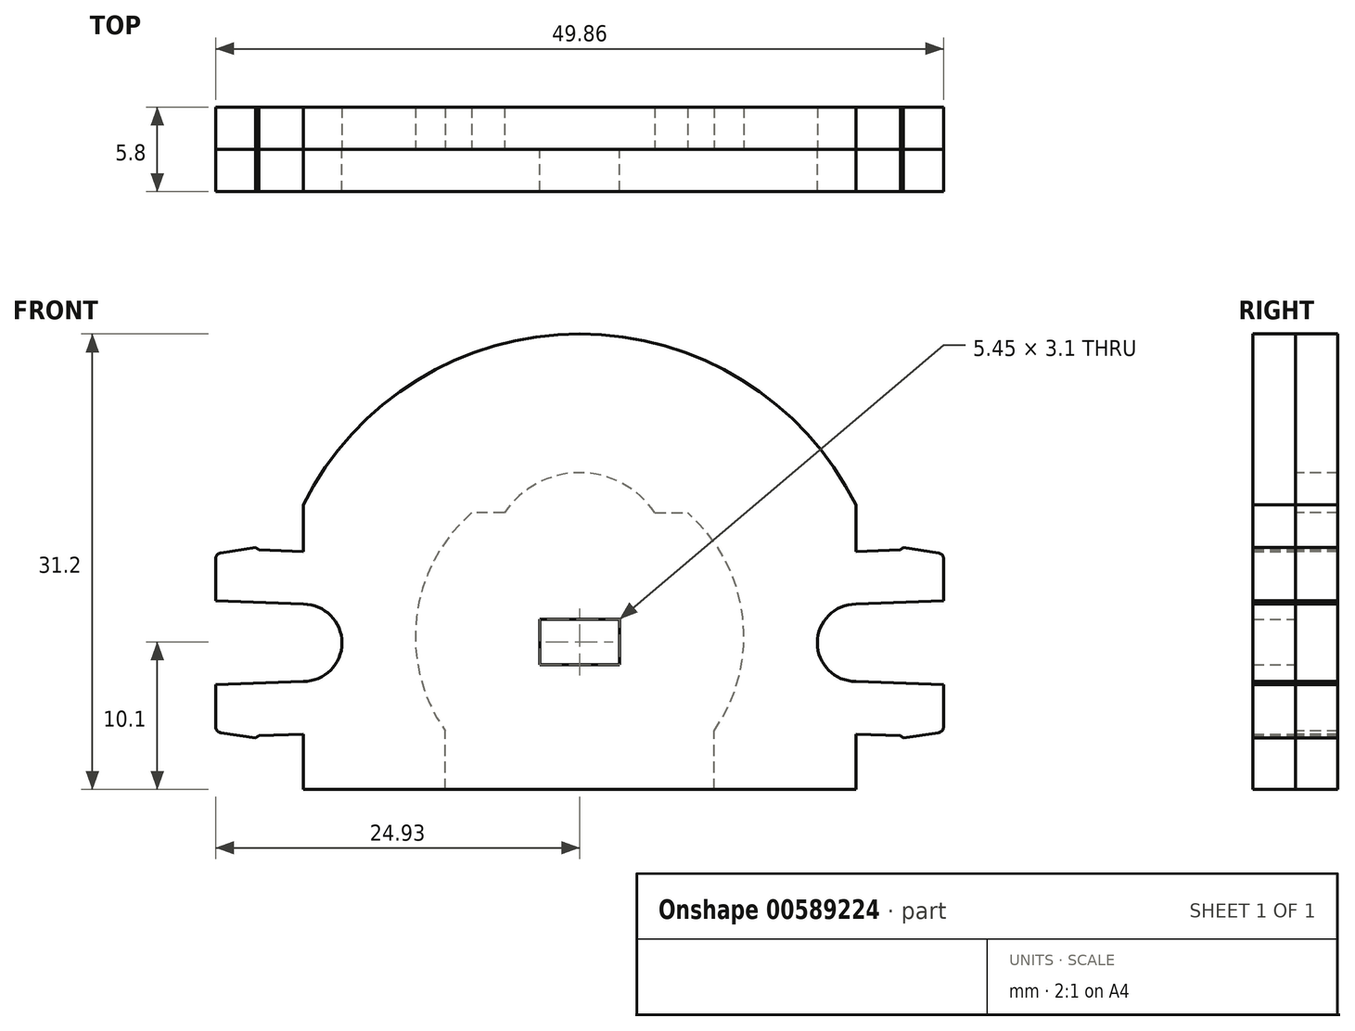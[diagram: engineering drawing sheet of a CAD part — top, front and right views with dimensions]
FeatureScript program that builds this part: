
annotation { "Feature Type Name" : "Feature", "Feature Type Description" : "" }
export const myFeature = defineFeature(function(context is Context, id is Id, definition is map)
    precondition{}
    {
        {
            var Q0;
            Q0=qCreatedBy(makeId("Front.planeOp"),FACE);
            var sketch = newSketch(context, id + "F0", { "sketchPlane" : qUnion([Q0])});
            skLineSegment(sketch, "E0.bottom", {"start": v(-18.93, 0) * mm, "end": v(18.93, 0) * mm});
            skLineSegment(sketch, "E0.left", {"start": v(-18.93, 0) * mm, "end": v(-18.93, 3.8) * mm});
            skLineSegment(sketch, "E0.right", {"start": v(18.93, 0) * mm, "end": v(18.93, 3.8) * mm});
            skPoint(sketch, "E0.middle", {"position": v(0, 9.75) * mm});
            skArc(sketch, "E1", {"start": v(18.92, 19.5) * mm, "mid": v(0, 31.2) * mm, "end": v(-18.93, 19.5) * mm});
            skLineSegment(sketch, "E2.bottom", {"start": v(-2.73, 11.65) * mm, "end": v(2.72, 11.65) * mm});
            skLineSegment(sketch, "E2.top", {"start": v(-2.73, 8.55) * mm, "end": v(2.72, 8.55) * mm});
            skLineSegment(sketch, "E2.left", {"start": v(-2.73, 11.65) * mm, "end": v(-2.73, 8.55) * mm});
            skLineSegment(sketch, "E2.right", {"start": v(2.72, 11.65) * mm, "end": v(2.72, 8.55) * mm});
            skPoint(sketch, "E2.middle", {"position": v(0, 10.1) * mm});
            skArc(sketch, "E3", {"start": v(-18.93, 7.4) * mm, "mid": v(-16.28, 10.04) * mm, "end": v(-18.93, 12.7) * mm});
            skLineSegment(sketch, "E4", {"start": v(-18.93, 12.7) * mm, "end": v(-24.93, 12.92) * mm});
            skLineSegment(sketch, "E5", {"start": v(-24.93, 12.92) * mm, "end": v(-24.93, 15.8) * mm});
            skLineSegment(sketch, "E6", {"start": v(-24.59, 16.2) * mm, "end": v(-22.18, 16.57) * mm});
            skLineSegment(sketch, "E7", {"start": v(-22.18, 16.57) * mm, "end": v(-21.98, 16.41) * mm});
            skLineSegment(sketch, "E8", {"start": v(-21.98, 16.41) * mm, "end": v(-18.92, 16.3) * mm});
            skPoint(sketch, "E9.visualSharp", {"position": v(-24.93, 16.14) * mm});
            skArc(sketch, "E9.filletArc", {"start": v(-24.59, 16.2) * mm, "mid": v(-24.83, 16.06) * mm, "end": v(-24.93, 15.8) * mm});
            skLineSegment(sketch, "E10", {"start": v(-18.93, 10.04) * mm, "end": v(-12.58, 10.04) * mm, "construction": true});
            skLineSegment(sketch, "E11.trimOffspring", {"start": v(-18.93, 16.3) * mm, "end": v(-18.93, 19.5) * mm});
            skLineSegment(sketch, "E12.MirrorCS", {"start": v(-22.18, 3.52) * mm, "end": v(-21.98, 3.68) * mm});
            skArc(sketch, "E13.MirrorCS", {"start": v(-24.59, 3.9) * mm, "mid": v(-24.83, 4.03) * mm, "end": v(-24.93, 4.29) * mm});
            skLineSegment(sketch, "E14.MirrorCS", {"start": v(-21.98, 3.68) * mm, "end": v(-18.92, 3.8) * mm});
            skLineSegment(sketch, "E15.MirrorCS", {"start": v(-18.93, 7.4) * mm, "end": v(-24.93, 7.17) * mm});
            skPoint(sketch, "E16.MirrorP", {"position": v(-24.93, 3.94) * mm});
            skLineSegment(sketch, "E17.MirrorCS", {"start": v(-24.59, 3.9) * mm, "end": v(-22.18, 3.52) * mm});
            skLineSegment(sketch, "E18.MirrorCS", {"start": v(-24.93, 7.17) * mm, "end": v(-24.93, 4.29) * mm});
            skLineSegment(sketch, "E19.MirrorCS", {"start": v(22.18, 16.57) * mm, "end": v(21.98, 16.41) * mm});
            skLineSegment(sketch, "E20.MirrorCS", {"start": v(22.18, 3.52) * mm, "end": v(21.98, 3.68) * mm});
            skLineSegment(sketch, "E21.MirrorCS", {"start": v(24.59, 16.2) * mm, "end": v(22.18, 16.57) * mm});
            skArc(sketch, "E22.MirrorCS", {"start": v(24.59, 16.2) * mm, "mid": v(24.83, 16.06) * mm, "end": v(24.93, 15.8) * mm});
            skLineSegment(sketch, "E23.MirrorCS", {"start": v(24.59, 3.9) * mm, "end": v(22.18, 3.52) * mm});
            skArc(sketch, "E24.MirrorCS", {"start": v(24.59, 3.9) * mm, "mid": v(24.83, 4.03) * mm, "end": v(24.93, 4.29) * mm});
            skLineSegment(sketch, "E25.MirrorCS", {"start": v(24.93, 12.92) * mm, "end": v(24.93, 15.8) * mm});
            skLineSegment(sketch, "E26.MirrorCS", {"start": v(24.93, 7.17) * mm, "end": v(24.93, 4.29) * mm});
            skLineSegment(sketch, "E27.MirrorCS", {"start": v(21.98, 16.41) * mm, "end": v(18.92, 16.3) * mm});
            skLineSegment(sketch, "E28.MirrorCS", {"start": v(18.93, 12.7) * mm, "end": v(24.93, 12.92) * mm});
            skPoint(sketch, "E29.MirrorP", {"position": v(24.93, 16.14) * mm});
            skLineSegment(sketch, "E30.MirrorCS", {"start": v(18.93, 7.4) * mm, "end": v(24.93, 7.17) * mm});
            skPoint(sketch, "E31.MirrorP", {"position": v(24.93, 3.94) * mm});
            skLineSegment(sketch, "E32.MirrorCS", {"start": v(21.98, 3.68) * mm, "end": v(18.92, 3.8) * mm});
            skArc(sketch, "E33.MirrorCS", {"start": v(18.93, 7.4) * mm, "mid": v(16.28, 10.04) * mm, "end": v(18.93, 12.7) * mm});
            skLineSegment(sketch, "E34.trimOffspring", {"start": v(18.93, 16.3) * mm, "end": v(18.93, 19.5) * mm});
            skSolve(sketch);
        }
        {
            var Q0;
            Q0=makeQuery(id+"F0.imprint","IMPRINT",FACE,{"disambiguationData":[TD([[makeQuery(id+"F0.imprint","IMPRINT",EDGE,{"derivedFrom":sQuery(id+"F0.wireOp",EDGE,"E0.bottom")}),1.0]])]});
            extrude(context, id + "F1", {"entities" : qUnion([Q0]), "depth" : 2.9 * mm, "offsetDistance" : 25 * mm});
        }
        {
            var Q0;
            Q0=qCreatedBy(makeId("Front.planeOp"),FACE);
            var sketch = newSketch(context, id + "F2", { "sketchPlane" : qUnion([Q0])});
            skArc(sketch, "E35.0", {"start": v(18.92, 19.5) * mm, "mid": v(0, 31.2) * mm, "end": v(-18.93, 19.5) * mm});
            skLineSegment(sketch, "E36.0", {"start": v(18.93, 16.3) * mm, "end": v(18.93, 19.5) * mm});
            skLineSegment(sketch, "E37.0", {"start": v(21.98, 16.41) * mm, "end": v(18.92, 16.3) * mm});
            skLineSegment(sketch, "E38.0.0", {"start": v(18.92, 16.3) * mm, "end": v(21.98, 16.41) * mm});
            skLineSegment(sketch, "E38.0.1", {"start": v(21.98, 16.41) * mm, "end": v(22.18, 16.57) * mm});
            skLineSegment(sketch, "E38.0.2", {"start": v(22.18, 16.57) * mm, "end": v(24.59, 16.2) * mm});
            skArc(sketch, "E38.0.3", {"start": v(24.59, 16.2) * mm, "mid": v(24.83, 16.06) * mm, "end": v(24.93, 15.8) * mm});
            skLineSegment(sketch, "E38.0.4", {"start": v(24.93, 15.8) * mm, "end": v(24.93, 12.92) * mm});
            skLineSegment(sketch, "E38.0.5", {"start": v(24.93, 12.92) * mm, "end": v(18.93, 12.7) * mm});
            skArc(sketch, "E38.0.6", {"start": v(18.93, 12.7) * mm, "mid": v(16.28, 10.04) * mm, "end": v(18.93, 7.4) * mm});
            skLineSegment(sketch, "E38.0.7", {"start": v(18.93, 7.4) * mm, "end": v(24.93, 7.17) * mm});
            skLineSegment(sketch, "E38.0.8", {"start": v(24.93, 7.17) * mm, "end": v(24.93, 4.29) * mm});
            skArc(sketch, "E38.0.9", {"start": v(24.93, 4.29) * mm, "mid": v(24.83, 4.03) * mm, "end": v(24.59, 3.9) * mm});
            skLineSegment(sketch, "E38.0.10", {"start": v(24.59, 3.9) * mm, "end": v(22.18, 3.52) * mm});
            skLineSegment(sketch, "E38.0.11", {"start": v(22.18, 3.52) * mm, "end": v(21.98, 3.68) * mm});
            skLineSegment(sketch, "E38.0.12", {"start": v(21.98, 3.68) * mm, "end": v(18.93, 3.8) * mm});
            skLineSegment(sketch, "E38.0.13", {"start": v(18.93, 3.8) * mm, "end": v(18.93, 0) * mm});
            skLineSegment(sketch, "E38.0.14", {"start": v(18.93, 0) * mm, "end": v(9.2, 0) * mm});
            skLineSegment(sketch, "E38.0.15", {"start": v(-18.93, 0) * mm, "end": v(-18.93, 3.8) * mm});
            skLineSegment(sketch, "E38.0.16", {"start": v(-18.93, 3.8) * mm, "end": v(-21.98, 3.68) * mm});
            skLineSegment(sketch, "E38.0.17", {"start": v(-21.98, 3.68) * mm, "end": v(-22.18, 3.52) * mm});
            skLineSegment(sketch, "E38.0.18", {"start": v(-22.18, 3.52) * mm, "end": v(-24.59, 3.9) * mm});
            skArc(sketch, "E38.0.19", {"start": v(-24.59, 3.9) * mm, "mid": v(-24.83, 4.03) * mm, "end": v(-24.93, 4.29) * mm});
            skLineSegment(sketch, "E38.0.20", {"start": v(-24.93, 4.29) * mm, "end": v(-24.93, 7.17) * mm});
            skLineSegment(sketch, "E38.0.21", {"start": v(-24.93, 7.17) * mm, "end": v(-18.93, 7.4) * mm});
            skArc(sketch, "E38.0.22", {"start": v(-18.93, 7.4) * mm, "mid": v(-16.28, 10.04) * mm, "end": v(-18.93, 12.7) * mm});
            skLineSegment(sketch, "E38.0.23", {"start": v(-18.93, 12.7) * mm, "end": v(-24.93, 12.92) * mm});
            skLineSegment(sketch, "E38.0.24", {"start": v(-24.93, 12.92) * mm, "end": v(-24.93, 15.8) * mm});
            skArc(sketch, "E38.0.25", {"start": v(-24.93, 15.8) * mm, "mid": v(-24.83, 16.06) * mm, "end": v(-24.59, 16.2) * mm});
            skLineSegment(sketch, "E38.0.26", {"start": v(-24.59, 16.2) * mm, "end": v(-22.18, 16.57) * mm});
            skLineSegment(sketch, "E38.0.27", {"start": v(-22.18, 16.57) * mm, "end": v(-21.98, 16.41) * mm});
            skLineSegment(sketch, "E38.0.28", {"start": v(-21.98, 16.41) * mm, "end": v(-18.92, 16.3) * mm});
            skLineSegment(sketch, "E38.0.29", {"start": v(-18.93, 16.3) * mm, "end": v(-18.93, 19.5) * mm});
            skArc(sketch, "E38.0.30", {"start": v(-18.93, 19.5) * mm, "mid": v(0, 31.2) * mm, "end": v(18.92, 19.5) * mm});
            skLineSegment(sketch, "E38.0.31", {"start": v(18.93, 19.5) * mm, "end": v(18.93, 16.3) * mm});
            skLineSegment(sketch, "E39", {"start": v(9.2, 0) * mm, "end": v(9.2, 4) * mm});
            skArc(sketch, "E40", {"start": v(5.15, 18.95) * mm, "mid": v(0, 21.7) * mm, "end": v(-5.15, 18.95) * mm});
            skPoint(sketch, "E41", {"position": v(0, 21.7) * mm});
            skLineSegment(sketch, "E42", {"start": v(-5.15, 18.95) * mm, "end": v(-7.4, 18.95) * mm});
            skLineSegment(sketch, "E43.MirrorCS", {"start": v(5.15, 18.95) * mm, "end": v(7.4, 18.95) * mm});
            skArc(sketch, "E44", {"start": v(-7.4, 18.95) * mm, "mid": v(-11.17, 11.82) * mm, "end": v(-9.2, 4) * mm});
            skLineSegment(sketch, "E45.MirrorCS", {"start": v(-9.2, 0) * mm, "end": v(-9.2, 4) * mm});
            skArc(sketch, "E46.trimOffspring", {"start": v(9.2, 4) * mm, "mid": v(11.17, 11.82) * mm, "end": v(7.4, 18.95) * mm});
            skLineSegment(sketch, "E47.trimOffspring", {"start": v(-9.2, 0) * mm, "end": v(-18.93, 0) * mm});
            skSolve(sketch);
        }
        {
            var Q0;
            Q0 = qSketchRegion(id + "F2", true);
            extrude(context, id + "F3", {"entities" : qUnion([Q0]), "oppositeDirection" : true, "depth" : 2.9 * mm, "offsetDistance" : 25 * mm});
        }
    });
